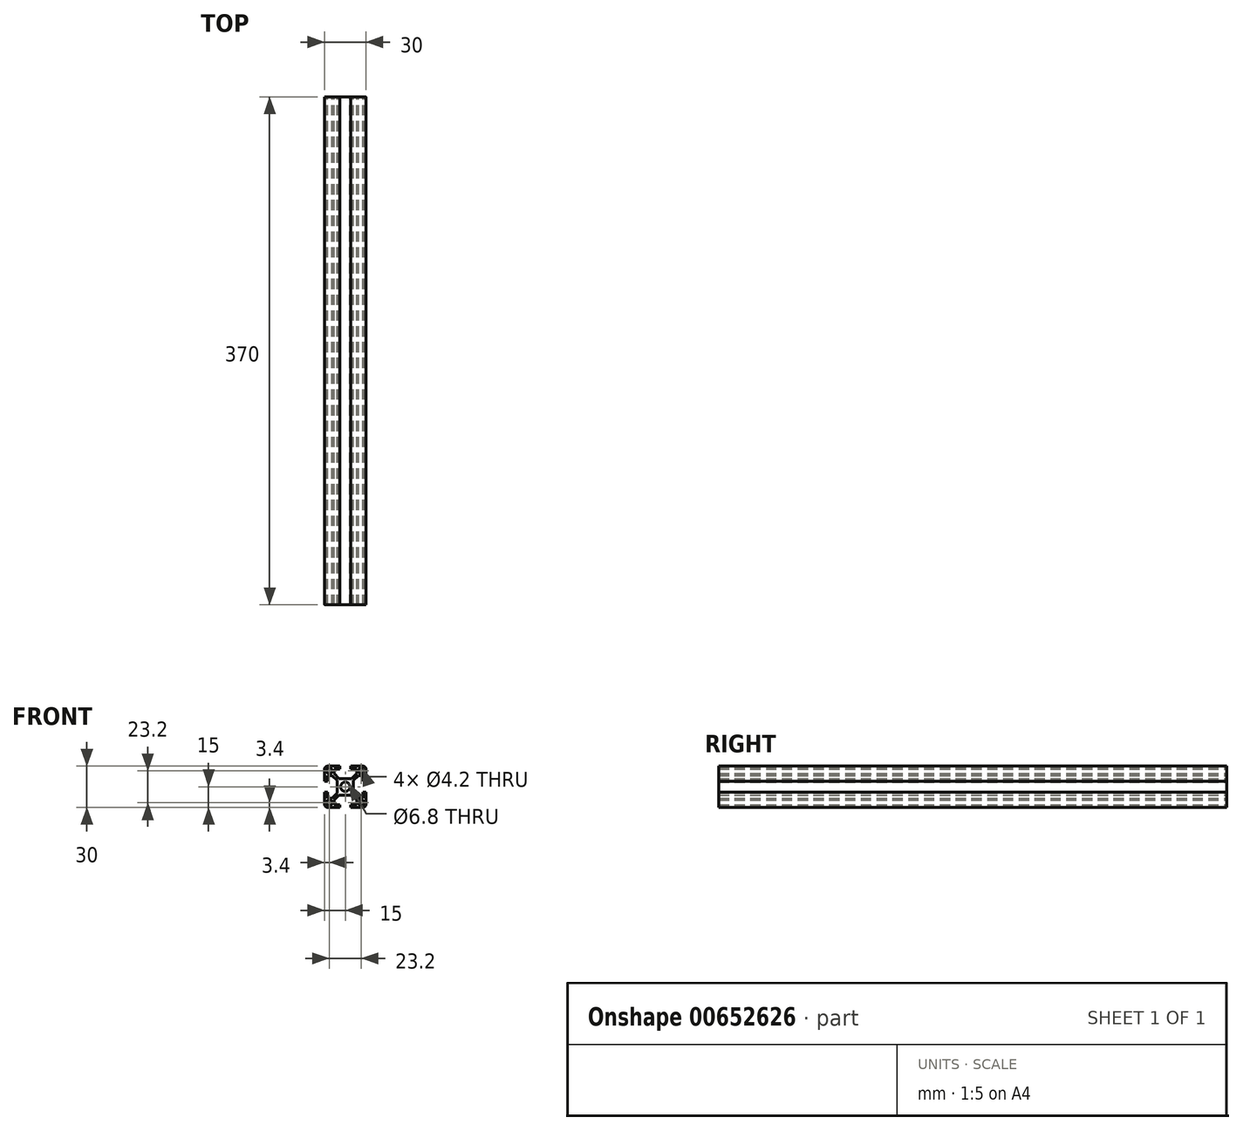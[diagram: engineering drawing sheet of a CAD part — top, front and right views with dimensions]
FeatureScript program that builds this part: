
annotation { "Feature Type Name" : "Feature", "Feature Type Description" : "" }
export const myFeature = defineFeature(function(context is Context, id is Id, definition is map)
    precondition{}
    {
        {
            var Q0;
            Q0=qCreatedBy(makeId("Front.planeOp"),FACE);
            var sketch = newSketch(context, id + "F0", { "sketchPlane" : qUnion([Q0])});
            skLineSegment(sketch, "E0", {"start": v(0, 6) * mm, "end": v(-4.59, 6) * mm});
            skLineSegment(sketch, "E1", {"start": v(-4.59, 6) * mm, "end": v(-8.25, 9.66) * mm});
            skLineSegment(sketch, "E2", {"start": v(-8.25, 9.66) * mm, "end": v(-8.25, 13) * mm});
            skLineSegment(sketch, "E3", {"start": v(-8.25, 13) * mm, "end": v(-4, 13) * mm});
            skLineSegment(sketch, "E4", {"start": v(-4, 13) * mm, "end": v(-4, 15) * mm});
            skLineSegment(sketch, "E5", {"start": v(-4, 15) * mm, "end": v(-13, 15) * mm});
            skLineSegment(sketch, "E6", {"start": v(-15, 13) * mm, "end": v(-15, 4) * mm});
            skLineSegment(sketch, "E7", {"start": v(-15, 4) * mm, "end": v(-13, 4) * mm});
            skLineSegment(sketch, "E8", {"start": v(-13, 4) * mm, "end": v(-13, 8.25) * mm});
            skLineSegment(sketch, "E9", {"start": v(-13, 8.25) * mm, "end": v(-9.66, 8.25) * mm});
            skLineSegment(sketch, "E10", {"start": v(-9.66, 8.25) * mm, "end": v(-6, 4.59) * mm});
            skLineSegment(sketch, "E11", {"start": v(-6, 4.59) * mm, "end": v(-6, 0) * mm});
            skLineSegment(sketch, "E12", {"start": v(-6, 0) * mm, "end": v(0, 0) * mm, "construction": true});
            skLineSegment(sketch, "E13", {"start": v(0, 0) * mm, "end": v(0, 6) * mm, "construction": true});
            skArc(sketch, "E14", {"start": v(0, 3.4) * mm, "mid": v(-2.4, 2.4) * mm, "end": v(-3.4, 0) * mm});
            skCircle(sketch, "E15", {"center": v(-11.6, 11.6) * mm, "radius": 2.1 * mm});
            skLineSegment(sketch, "E16", {"start": v(0, 0) * mm, "end": v(-7.38, 7.38) * mm, "construction": true});
            skLineSegment(sketch, "E17.1.0", {"start": v(-8.25, -13) * mm, "end": v(-8.25, -9.66) * mm});
            skLineSegment(sketch, "E17.1.1", {"start": v(-4, -15) * mm, "end": v(-4, -13) * mm});
            skLineSegment(sketch, "E17.1.2", {"start": v(-4, -13) * mm, "end": v(-8.25, -13) * mm});
            skLineSegment(sketch, "E17.1.3", {"start": v(-15, -4) * mm, "end": v(-15, -13) * mm});
            skLineSegment(sketch, "E17.1.4", {"start": v(-8.25, -9.66) * mm, "end": v(-4.59, -6) * mm});
            skLineSegment(sketch, "E17.1.5", {"start": v(-13, -15) * mm, "end": v(-4, -15) * mm});
            skLineSegment(sketch, "E17.1.6", {"start": v(-4.59, -6) * mm, "end": v(0, -6) * mm});
            skLineSegment(sketch, "E17.1.7", {"start": v(0, -6) * mm, "end": v(0, 0) * mm, "construction": true});
            skLineSegment(sketch, "E17.1.8", {"start": v(0, 0) * mm, "end": v(-6, 0) * mm, "construction": true});
            skLineSegment(sketch, "E17.1.9", {"start": v(-13, -4) * mm, "end": v(-15, -4) * mm});
            skLineSegment(sketch, "E17.1.10", {"start": v(-13, -8.25) * mm, "end": v(-13, -4) * mm});
            skArc(sketch, "E17.1.11", {"start": v(-3.4, 0) * mm, "mid": v(-2.4, -2.4) * mm, "end": v(0, -3.4) * mm});
            skLineSegment(sketch, "E17.1.12", {"start": v(-9.66, -8.25) * mm, "end": v(-13, -8.25) * mm});
            skLineSegment(sketch, "E17.1.13", {"start": v(0, 0) * mm, "end": v(-7.38, -7.38) * mm, "construction": true});
            skLineSegment(sketch, "E17.1.14", {"start": v(-6, -4.59) * mm, "end": v(-9.66, -8.25) * mm});
            skCircle(sketch, "E17.1.15", {"center": v(-11.6, -11.6) * mm, "radius": 2.1 * mm});
            skLineSegment(sketch, "E17.1.16", {"start": v(-6, 0) * mm, "end": v(-6, -4.59) * mm});
            skLineSegment(sketch, "E17.2.0", {"start": v(13, -8.25) * mm, "end": v(9.66, -8.25) * mm});
            skLineSegment(sketch, "E17.2.1", {"start": v(15, -4) * mm, "end": v(13, -4) * mm});
            skLineSegment(sketch, "E17.2.2", {"start": v(13, -4) * mm, "end": v(13, -8.25) * mm});
            skLineSegment(sketch, "E17.2.3", {"start": v(4, -15) * mm, "end": v(13, -15) * mm});
            skLineSegment(sketch, "E17.2.4", {"start": v(9.66, -8.25) * mm, "end": v(6, -4.59) * mm});
            skLineSegment(sketch, "E17.2.5", {"start": v(15, -13) * mm, "end": v(15, -4) * mm});
            skLineSegment(sketch, "E17.2.6", {"start": v(6, -4.59) * mm, "end": v(6, 0) * mm});
            skLineSegment(sketch, "E17.2.7", {"start": v(6, 0) * mm, "end": v(0, 0) * mm, "construction": true});
            skLineSegment(sketch, "E17.2.8", {"start": v(0, 0) * mm, "end": v(0, -6) * mm, "construction": true});
            skLineSegment(sketch, "E17.2.9", {"start": v(4, -13) * mm, "end": v(4, -15) * mm});
            skLineSegment(sketch, "E17.2.10", {"start": v(8.25, -13) * mm, "end": v(4, -13) * mm});
            skArc(sketch, "E17.2.11", {"start": v(0, -3.4) * mm, "mid": v(2.4, -2.4) * mm, "end": v(3.4, 0) * mm});
            skLineSegment(sketch, "E17.2.12", {"start": v(8.25, -9.66) * mm, "end": v(8.25, -13) * mm});
            skLineSegment(sketch, "E17.2.13", {"start": v(0, 0) * mm, "end": v(7.38, -7.38) * mm, "construction": true});
            skLineSegment(sketch, "E17.2.14", {"start": v(4.59, -6) * mm, "end": v(8.25, -9.66) * mm});
            skCircle(sketch, "E17.2.15", {"center": v(11.6, -11.6) * mm, "radius": 2.1 * mm});
            skLineSegment(sketch, "E17.2.16", {"start": v(0, -6) * mm, "end": v(4.59, -6) * mm});
            skLineSegment(sketch, "E17.3.0", {"start": v(8.25, 13) * mm, "end": v(8.25, 9.66) * mm});
            skLineSegment(sketch, "E17.3.1", {"start": v(4, 15) * mm, "end": v(4, 13) * mm});
            skLineSegment(sketch, "E17.3.2", {"start": v(4, 13) * mm, "end": v(8.25, 13) * mm});
            skLineSegment(sketch, "E17.3.3", {"start": v(15, 4) * mm, "end": v(15, 13) * mm});
            skLineSegment(sketch, "E17.3.4", {"start": v(8.25, 9.66) * mm, "end": v(4.59, 6) * mm});
            skLineSegment(sketch, "E17.3.5", {"start": v(13, 15) * mm, "end": v(4, 15) * mm});
            skLineSegment(sketch, "E17.3.6", {"start": v(4.59, 6) * mm, "end": v(0, 6) * mm});
            skLineSegment(sketch, "E17.3.7", {"start": v(0, 6) * mm, "end": v(0, 0) * mm, "construction": true});
            skLineSegment(sketch, "E17.3.8", {"start": v(0, 0) * mm, "end": v(6, 0) * mm, "construction": true});
            skLineSegment(sketch, "E17.3.9", {"start": v(13, 4) * mm, "end": v(15, 4) * mm});
            skLineSegment(sketch, "E17.3.10", {"start": v(13, 8.25) * mm, "end": v(13, 4) * mm});
            skArc(sketch, "E17.3.11", {"start": v(3.4, 0) * mm, "mid": v(2.4, 2.4) * mm, "end": v(0, 3.4) * mm});
            skLineSegment(sketch, "E17.3.12", {"start": v(9.66, 8.25) * mm, "end": v(13, 8.25) * mm});
            skLineSegment(sketch, "E17.3.13", {"start": v(0, 0) * mm, "end": v(7.38, 7.38) * mm, "construction": true});
            skLineSegment(sketch, "E17.3.14", {"start": v(6, 4.59) * mm, "end": v(9.66, 8.25) * mm});
            skCircle(sketch, "E17.3.15", {"center": v(11.6, 11.6) * mm, "radius": 2.1 * mm});
            skLineSegment(sketch, "E17.3.16", {"start": v(6, 0) * mm, "end": v(6, 4.59) * mm});
            skPoint(sketch, "E18.visualSharp", {"position": v(-15, 15) * mm});
            skArc(sketch, "E18.filletArc", {"start": v(-13, 15) * mm, "mid": v(-14.41, 14.41) * mm, "end": v(-15, 13) * mm});
            skPoint(sketch, "E19.visualSharp", {"position": v(15, 15) * mm});
            skArc(sketch, "E19.filletArc", {"start": v(15, 13) * mm, "mid": v(14.41, 14.41) * mm, "end": v(13, 15) * mm});
            skPoint(sketch, "E20.visualSharp", {"position": v(15, -15) * mm});
            skArc(sketch, "E20.filletArc", {"start": v(13, -15) * mm, "mid": v(14.41, -14.41) * mm, "end": v(15, -13) * mm});
            skPoint(sketch, "E21.visualSharp", {"position": v(-15, -15) * mm});
            skArc(sketch, "E21.filletArc", {"start": v(-15, -13) * mm, "mid": v(-14.41, -14.41) * mm, "end": v(-13, -15) * mm});
            skSolve(sketch);
        }
        {
            var Q0;
            Q0 = qSketchRegion(id + "F0", true);
            extrude(context, id + "F1", {"entities" : qUnion([Q0]), "depth" : 370 * mm, "offsetDistance" : 25 * mm});
        }
    });
